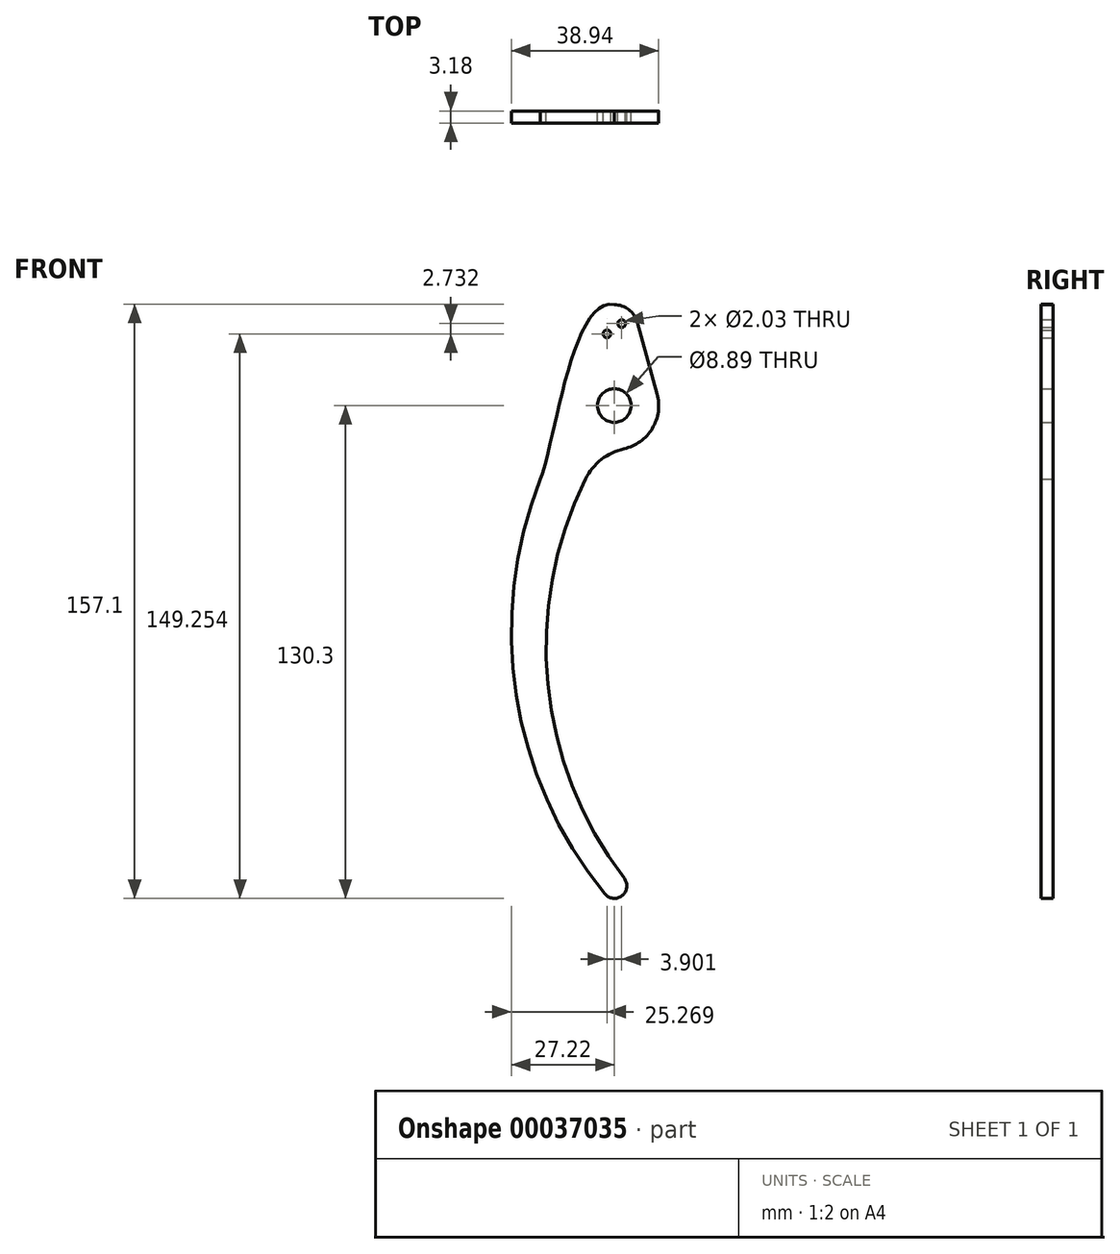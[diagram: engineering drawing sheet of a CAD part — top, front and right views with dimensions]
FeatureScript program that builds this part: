
annotation { "Feature Type Name" : "Feature", "Feature Type Description" : "" }
export const myFeature = defineFeature(function(context is Context, id is Id, definition is map)
    precondition{}
    {
        {
            var Q0;
            Q0=qCreatedBy(makeId("Front.planeOp"),FACE);
            var sketch = newSketch(context, id + "F0", { "sketchPlane" : qUnion([Q0])});
            skLineSegment(sketch, "E0", {"start": v(0, 0) * mm, "end": v(0, -127) * mm, "construction": true});
            skLineSegment(sketch, "E1", {"start": v(0, 0) * mm, "end": v(0, 20.32) * mm, "construction": true});
            skLineSegment(sketch, "E2", {"start": v(6.12, 22) * mm, "end": v(11.3, 3.1) * mm});
            skArc(sketch, "E3", {"start": v(11.3, 3.1) * mm, "mid": v(10.04, -6.05) * mm, "end": v(2.54, -11.44) * mm});
            skArc(sketch, "E4", {"start": v(-2.56, -129.09) * mm, "mid": v(2.05, -129.6) * mm, "end": v(2.62, -125) * mm});
            skArc(sketch, "E5", {"start": v(-2.56, -129.09) * mm, "mid": v(-25.93, -76.55) * mm, "end": v(-19.53, -19.41) * mm});
            skCircle(sketch, "E6", {"center": v(0, 0) * mm, "radius": 4.45 * mm});
            skArc(sketch, "E7", {"start": v(2.54, -11.44) * mm, "mid": v(-3.45, -14.27) * mm, "end": v(-7.62, -19.41) * mm});
            skArc(sketch, "E8", {"start": v(-7.62, -19.41) * mm, "mid": v(-17.55, -73.66) * mm, "end": v(2.62, -125) * mm});
            skLineSegment(sketch, "E9", {"start": v(-1.95, 18.95) * mm, "end": v(1.95, 21.69) * mm, "construction": true});
            skCircle(sketch, "E10", {"center": v(-1.95, 18.95) * mm, "radius": 1.02 * mm});
            skCircle(sketch, "E11", {"center": v(1.95, 21.69) * mm, "radius": 1.02 * mm});
            skLineSegment(sketch, "E12", {"start": v(0, 0) * mm, "end": v(11.3, 0) * mm});
            skLineSegment(sketch, "E13", {"start": v(0, 0) * mm, "end": v(-9.52, 0) * mm});
            skArc(sketch, "E14", {"start": v(6.12, 22) * mm, "mid": v(3.85, 25.37) * mm, "end": v(0, 26.67) * mm});
            skLineSegment(sketch, "E15", {"start": v(-7.62, -19.41) * mm, "end": v(-19.53, -19.41) * mm});
            skFitSpline(sketch, "E16", {"points": [v(0, 26.67) * mm, v(-19.53, -19.41) * mm], "startDerivative": vector(-33.74, 8.14) * mm, "endDerivative": vector(-10.66, -24.9) * mm});
            skSolve(sketch);
        }
        {
            var Q0;
            Q0=qSketchRegion(id+"F0",true);
            extrude(context, id + "F1", {"entities" : qUnion([Q0]), "depth" : 3.17 * mm});
        }
    });
